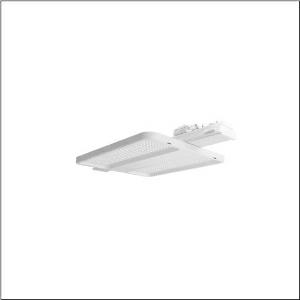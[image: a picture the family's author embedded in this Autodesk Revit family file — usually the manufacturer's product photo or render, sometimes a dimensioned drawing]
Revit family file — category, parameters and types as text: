
# Revit family: highbay_11_fur_licross_r__tragschiene_midi_51hn11da4mla02_c32c
name_source: partatom
category: Lighting Fixtures
units: mm (PartAtom-declared; Revit-internal decimal feet)

## family parameters
Cut with Voids When Loaded = No
Host = Face
Light Source = No
Part Type = Normal
Room Calculation Point = No
Round Connector Dimension = Use Diameter
Shared = No

## types (1)
- --- (1 x LED, 28000 lm, 147.1 W, 4000K)
    Apparent Load = 147 VA
    CIE Flux Codes = 85 97 100 100 100
    Color Rendering = 80
    Color Temperature = 4000K
    Default Elevation = 1800 mm
    Description = high bay luminaire Highbay 11 for Licross® trunking rail midi; direct symmetric narrow distribution, light control with lens of PMMA; UGR ≤ 22 (X = 4H | Y = 8H | S = 0.25H | reflection values 70/50/20); luminous flux: 28.000lm; light colour: 840, colour temperature: 4000K, MacAdam ≤ 2 SDCM (initial), colour rendering: CRI > 80; luminous efficacy: 190,3lm/W; rated service life: 100.000h (L95/B50) at AT= 25°C; control: Bluetooth® Mesh; for wireless networking: Node luminaire for setting up a local control solution without a higher-level application controller, intelligence completely in the luminaire; no control line such as DALI between the Node multi-sensor luminaires and Nodes is required, wireless integration of other Node luminaires and Node multi-sensor luminaires into the network is possible; number of Node luminaires in the project can be expanded as required, network sizes > 300 Nodes can be realized; can also be connected to lighting or building automation via various gateways upon request; integrated DALI2 ECG provides luminaire data (according to IEC62386, Part 251), energy data (Part 252), and monitoring and analytics data (Part 253) to higher-level systems for further processing; luminaire connection: plug, 5-pole, with phase selectionmains connection: 230..240V, AC 50/60Hz; connected load: 147,1W; protection rating (complete): IP64; insulation class (complete): insulation class I (protective earthing); protection symbol: D; impact resistance: IK07; certification: CE, ENEC, VDE, UKCA; internal wiring halogen-free; luminaire corresponds to IFS (International Featured Standards) requirements for safety and quality in the food industry; LABS conformity tested according to VDMA 24364:2018-05; housing frame of high-performance plastic PA6, matt traffic white (RAL 9016); cover of PMMA; fixing on rail side of steel, galvanised, white; blank cover of PC/ABS, traffic white (RAL 9016); dimension (LxWxH): 750 x 442 x 72mm; permissible operating ambient temperature: -20..+35°C (reducing of maximum allowable ambient temperature of 5°C with ceiling mounting); packaging unit: 1 piece
    Height = 72 mm  [stored 0.23622 ft]
    Lamp = 1 x LED
    Lamp Light Flux = 28000 lm
    Lamp Power = 147.1 W
    Lamp count = 1
    Length = 474 mm
    Luminous efficacy = 190 lm/W
    Manufacturer = Siteco
    ModVariant = No
    Model = 51HN11DA4MLA02
    Mounting Place = Ceiling
    Mounting Type = Pendant
    Number of Poles = 1
    OnlyDefault = Yes
    Power Factor = 1
    Product Name = Highbay 11 für Licross® Tragschiene midi
    Product group = high bay luminaire
    ProductGroupID = 901
    Protection Class = Protection class I
    Protection Degree = IP 64
    RLX_Detail_Level = 1
    RLX_Emergency_Light_Flux = 0 lm
    RLX_Emergency_Type = 0
    RLX_Emergency_Type_DB = No
    RlxData = <blob elided: 18133 chars, md5=3e1d0f3a>
    Socket = socket
    Standby Power = 0 W
    System Light Flux = 28000 lm
    System Power = 147 W
    Type Comments = factory setting: luminous flux: 100 % | dim-lin: 254 | 661 mA
    Type Image = l_1363258.jpg
    URL = http://relux.com
    VarID = @adj_022209
    Voltage = 0 V
    Weight = 0.00 kg
    Width = 442 mm

note: [stored X ft] marks values corroborated as IEEE doubles in the binary element streams (Revit-internal decimal feet)

## geometry (parser evidence)
native form markers: Blend x4, Sweep x10
no freeform markers — native parametric forms only
